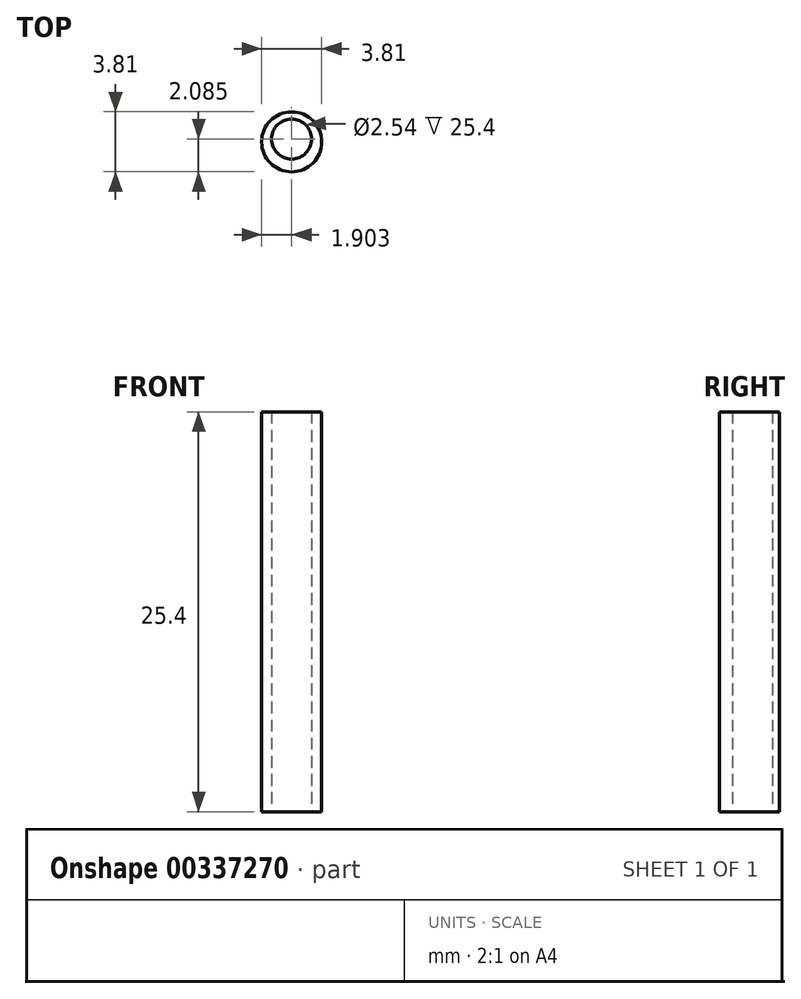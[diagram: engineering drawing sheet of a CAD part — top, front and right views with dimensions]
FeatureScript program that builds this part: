
annotation { "Feature Type Name" : "Feature", "Feature Type Description" : "" }
export const myFeature = defineFeature(function(context is Context, id is Id, definition is map)
    precondition{}
    {
        {
            var Q0;
            Q0=qCreatedBy(makeId("Top.planeOp"),FACE);
            var sketch = newSketch(context, id + "F0", { "sketchPlane" : qUnion([Q0])});
            skCircle(sketch, "E0", {"center": v(-49.4, 47.01) * mm, "radius": 1.9 * mm});
            skSolve(sketch);
        }
        {
            var Q0;
            Q0 = qSketchRegion(id + "F0", true);
            extrude(context, id + "F1", {"entities" : qUnion([Q0]), "depth" : 25.4 * mm});
        }
        {
            var Q0;
            Q0=qCreatedBy(makeId("Top.planeOp"),FACE);
            var sketch = newSketch(context, id + "F2", { "sketchPlane" : qUnion([Q0])});
            skPoint(sketch, "E1", {"position": v(-49.4, 47.2) * mm});
            skSolve(sketch);
        }
        {
            var Q0;
            Q0=sQuery(id+"F2.wireOp",VERTEX,"E1");
            var Q1;
            Q1=makeQuery(id+"F1.opExtrude","SWEPT_BODY",BODY,{"disambiguationData":[OSD([sQuery(id+"F0.wireOp",EDGE,"E0")])]});
            hole(context, id + "F3", {"style" : HoleStyle.SIMPLE, "endStyle" : HoleEndStyle.THROUGH, "oppositeDirection" : true, "holeDiameter" : 2.54 * mm, "tappedDepth" : 12.7 * mm, "tapClearance" : 3, "locations" : qUnion([Q0]), "scope" : qUnion([Q1])});
        }
    });
